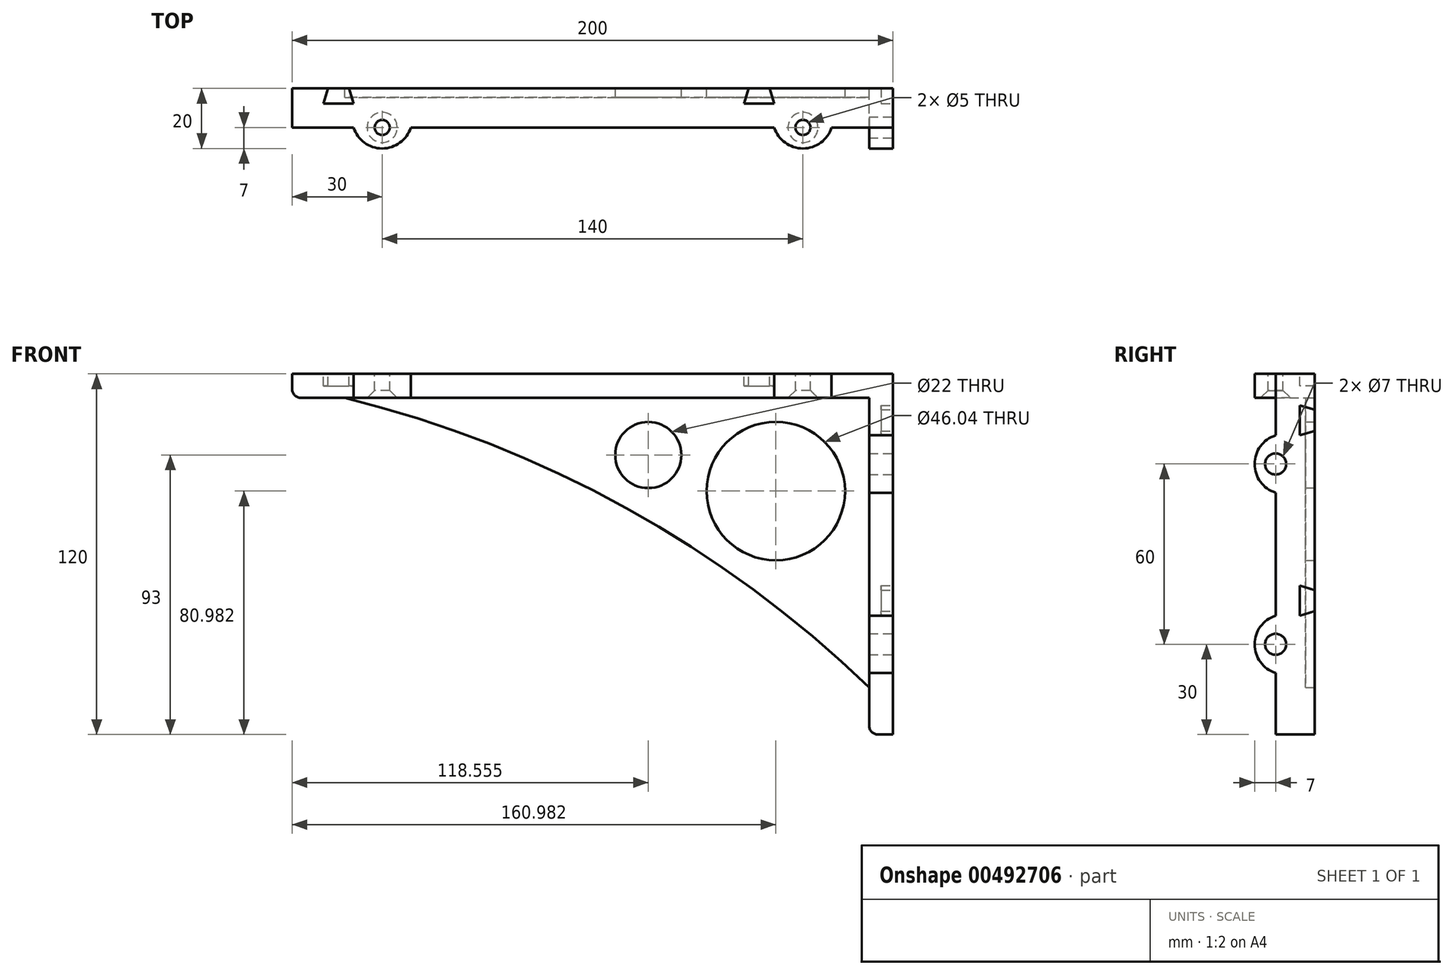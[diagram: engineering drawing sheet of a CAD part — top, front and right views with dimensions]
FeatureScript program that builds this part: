
annotation { "Feature Type Name" : "Feature", "Feature Type Description" : "" }
export const myFeature = defineFeature(function(context is Context, id is Id, definition is map)
    precondition{}
    {
        {
            var Q0;
            Q0=qCreatedBy(makeId("Front.planeOp"),FACE);
            var sketch = newSketch(context, id + "F0", { "sketchPlane" : qUnion([Q0])});
            skLineSegment(sketch, "E0", {"start": v(0, 150.58) * mm, "end": v(0, -150.58) * mm, "construction": true});
            skLineSegment(sketch, "E1", {"start": v(52, 0) * mm, "end": v(-5, 0) * mm, "construction": true});
            skLineSegment(sketch, "E2.bottom", {"start": v(-200, 120) * mm, "end": v(0, 120) * mm});
            skLineSegment(sketch, "E2.top", {"start": v(-197, 112) * mm, "end": v(-8, 112) * mm});
            skLineSegment(sketch, "E2.left", {"start": v(-200, 120) * mm, "end": v(-200, 115) * mm});
            skLineSegment(sketch, "E3.top", {"start": v(-8, 0) * mm, "end": v(0, 0) * mm});
            skLineSegment(sketch, "E3.left", {"start": v(-8, 112) * mm, "end": v(-8, 3) * mm});
            skLineSegment(sketch, "E4", {"start": v(0, 120) * mm, "end": v(0, 0) * mm});
            skCircle(sketch, "E5", {"center": v(-39.02, 80.98) * mm, "radius": 23.02 * mm});
            skLineSegment(sketch, "E6", {"start": v(0, 120) * mm, "end": v(-8, 112) * mm, "construction": true});
            skLineSegment(sketch, "E7", {"start": v(-8, 112) * mm, "end": v(-70.48, 49.52) * mm, "construction": true});
            skCircle(sketch, "E8", {"center": v(-81.45, 93) * mm, "radius": 11 * mm});
            skArc(sketch, "E9", {"start": v(-8, 15.64) * mm, "mid": v(-88.84, 75.38) * mm, "end": v(-182.45, 112) * mm});
            skPoint(sketch, "E10.visualSharp", {"position": v(-200, 112) * mm});
            skArc(sketch, "E10.filletArc", {"start": v(-200, 115) * mm, "mid": v(-199.12, 112.88) * mm, "end": v(-197, 112) * mm});
            skArc(sketch, "E11.filletArc", {"start": v(-8, 3) * mm, "mid": v(-7.12, 0.88) * mm, "end": v(-5, 0) * mm});
            skLineSegment(sketch, "E12", {"start": v(-210.09, 116) * mm, "end": v(15.72, 116) * mm, "construction": true});
            skLineSegment(sketch, "E13", {"start": v(-4, 123.59) * mm, "end": v(-4, 7.46) * mm, "construction": true});
            skPoint(sketch, "E13.endSnap0", {"position": v(-4, 0) * mm});
            skSolve(sketch);
        }
        {
            var Q0;
            Q0=makeQuery(id+"F0.imprint","IMPRINT",FACE,{"disambiguationData":[TD([[makeQuery(id+"F0.imprint","IMPRINT",EDGE,{"derivedFrom":sQuery(id+"F0.wireOp",EDGE,"E5")}),-1.0]])]});
            extrude(context, id + "F1", {"entities" : qUnion([Q0]), "depth" : 3 * mm});
        }
        {
            var Q0;
            Q0=makeQuery(id+"F0.imprint","IMPRINT",FACE,{"disambiguationData":[TD([[makeQuery(id+"F0.imprint","IMPRINT",EDGE,{"derivedFrom":sQuery(id+"F0.wireOp",EDGE,"E2.bottom")}),-1.0]])]});
            extrude(context, id + "F2", {"entities" : qUnion([Q0]), "depth" : 20 * mm});
        }
        {
            var Q0;
            Q0=qCreatedBy(makeId("Right.planeOp"),FACE);
            var sketch = newSketch(context, id + "F3", { "sketchPlane" : qUnion([Q0])});
            skLineSegment(sketch, "E14", {"start": v(0, 131.94) * mm, "end": v(0, -6.13) * mm, "construction": true});
            skLineSegment(sketch, "E15", {"start": v(28.25, 0) * mm, "end": v(-74.04, 0) * mm, "construction": true});
            skLineSegment(sketch, "E16", {"start": v(-10, 123.32) * mm, "end": v(-10, 3.6) * mm, "construction": true});
            skCircle(sketch, "E17", {"center": v(-10, 90) * mm, "radius": 10 * mm});
            skCircle(sketch, "E18.1.0.0", {"center": v(-10, 30) * mm, "radius": 10 * mm});
            skLineSegment(sketch, "E18.direction1", {"start": v(-10, 90) * mm, "end": v(-10, 30) * mm, "construction": true});
            skLineSegment(sketch, "E19", {"start": v(-13, 124.76) * mm, "end": v(-13, -7.06) * mm, "construction": true});
            skCircle(sketch, "E20", {"center": v(-13, 90) * mm, "radius": 3.5 * mm});
            skCircle(sketch, "E21", {"center": v(-13, 30) * mm, "radius": 3.5 * mm});
            skLineSegment(sketch, "E22.0", {"start": v(-20, 120) * mm, "end": v(0, 120) * mm});
            skLineSegment(sketch, "E23.0", {"start": v(-20, 120) * mm, "end": v(-20, 0) * mm});
            skLineSegment(sketch, "E24.0.0", {"start": v(0, 0) * mm, "end": v(0, 120) * mm});
            skLineSegment(sketch, "E24.0.1", {"start": v(0, 120) * mm, "end": v(-20, 120) * mm});
            skLineSegment(sketch, "E24.0.3", {"start": v(-20, 0) * mm, "end": v(0, 0) * mm});
            skLineSegment(sketch, "E25", {"start": v(-13, 120) * mm, "end": v(-13, 99.54) * mm});
            skLineSegment(sketch, "E26", {"start": v(-13, 80.46) * mm, "end": v(-13, 39.54) * mm});
            skLineSegment(sketch, "E27", {"start": v(-13, 20.46) * mm, "end": v(-13, 0) * mm});
            skSolve(sketch);
        }
        {
            var Q0;
            {var subQ0=sQuery(id+"F3.wireOp",EDGE,"E27");Q0=makeQuery(id+"F3.imprint","IMPRINT",FACE,{"disambiguationData":[TD([[makeQuery(id+"F3.imprint","IMPRINT",EDGE,{"derivedFrom":subQ0}),-1.0]])]});}
            var Q1;
            {var subQ0=sQuery(id+"F3.wireOp",EDGE,"E26");Q1=makeQuery(id+"F3.imprint","IMPRINT",FACE,{"disambiguationData":[TD([[makeQuery(id+"F3.imprint","IMPRINT",EDGE,{"derivedFrom":subQ0}),-1.0]])]});}
            var Q2;
            {var subQ0=sQuery(id+"F3.wireOp",EDGE,"E25");Q2=makeQuery(id+"F3.imprint","IMPRINT",FACE,{"disambiguationData":[TD([[makeQuery(id+"F3.imprint","IMPRINT",EDGE,{"derivedFrom":subQ0}),-1.0]])]});}
            var Q3;
            Q3=makeQuery(id+"F3.imprint","IMPRINT",FACE,{"disambiguationData":[TD([[makeQuery(id+"F3.imprint","IMPRINT",EDGE,{"derivedFrom":sQuery(id+"F3.wireOp",EDGE,"E20")}),1.0]])]});
            var Q4;
            Q4=makeQuery(id+"F3.imprint","IMPRINT",FACE,{"disambiguationData":[TD([[makeQuery(id+"F3.imprint","IMPRINT",EDGE,{"derivedFrom":sQuery(id+"F3.wireOp",EDGE,"E21")}),1.0]])]});
            extrude(context, id + "F4", {"entities" : qUnion([Q0, Q1, Q2, Q3, Q4]), "operationType" : NewBodyOperationType.REMOVE, "oppositeDirection" : true, "depth" : 10 * mm});
        }
        {
            var Q0;
            Q0=makeQuery(id+"F2.opExtrude","SWEPT_FACE",FACE,{"disambiguationData":[OSD([sQuery(id+"F0.wireOp",EDGE,"E4")])]});
            var sketch = newSketch(context, id + "F5", { "sketchPlane" : qUnion([Q0])});
            skLineSegment(sketch, "E28", {"start": v(0, 114.7) * mm, "end": v(0, -4.87) * mm, "construction": true});
            skLineSegment(sketch, "E29", {"start": v(-17.8, 0) * mm, "end": v(12.61, 0) * mm, "construction": true});
            skLineSegment(sketch, "E30", {"start": v(-13, 99.54) * mm, "end": v(6.7, 99.54) * mm, "construction": true});
            skLineSegment(sketch, "E31", {"start": v(-13, 39.54) * mm, "end": v(7.65, 39.54) * mm, "construction": true});
            skLineSegment(sketch, "E32", {"start": v(0, 108.04) * mm, "end": v(-5, 109.54) * mm});
            skLineSegment(sketch, "E33", {"start": v(-5, 109.54) * mm, "end": v(-5, 99.54) * mm});
            skLineSegment(sketch, "E34", {"start": v(-5, 99.54) * mm, "end": v(0, 101.04) * mm});
            skLineSegment(sketch, "E35", {"start": v(0, 108.04) * mm, "end": v(0, 101.04) * mm});
            skLineSegment(sketch, "E36", {"start": v(3.72, 104.54) * mm, "end": v(-16.38, 104.54) * mm, "construction": true});
            skLineSegment(sketch, "E37", {"start": v(0, 48.04) * mm, "end": v(-5, 49.54) * mm});
            skLineSegment(sketch, "E38", {"start": v(-5, 49.54) * mm, "end": v(-5, 39.54) * mm});
            skLineSegment(sketch, "E39", {"start": v(-5, 39.54) * mm, "end": v(0, 41.04) * mm});
            skLineSegment(sketch, "E40", {"start": v(0, 48.04) * mm, "end": v(0, 41.04) * mm});
            skLineSegment(sketch, "E41", {"start": v(1.78, 44.54) * mm, "end": v(-18.33, 44.54) * mm, "construction": true});
            skSolve(sketch);
        }
        {
            var Q0;
            Q0=makeQuery(id+"F5.imprint","IMPRINT",FACE,{"disambiguationData":[TD([[makeQuery(id+"F5.imprint","IMPRINT",EDGE,{"derivedFrom":sQuery(id+"F5.wireOp",EDGE,"E32")}),1.0]])]});
            var Q1;
            Q1=makeQuery(id+"F5.imprint","IMPRINT",FACE,{"disambiguationData":[TD([[makeQuery(id+"F5.imprint","IMPRINT",EDGE,{"derivedFrom":sQuery(id+"F5.wireOp",EDGE,"E37")}),1.0]])]});
            extrude(context, id + "F6", {"entities" : qUnion([Q0, Q1]), "operationType" : NewBodyOperationType.REMOVE, "oppositeDirection" : true, "depth" : 4 * mm});
        }
        {
            var Q0;
            Q0=makeQuery(id+"F2.opExtrude","SWEPT_FACE",FACE,{"disambiguationData":[OSD([sQuery(id+"F0.wireOp",EDGE,"E2.bottom")])]});
            var sketch = newSketch(context, id + "F7", { "sketchPlane" : qUnion([Q0])});
            skLineSegment(sketch, "E42", {"start": v(-215.12, 0) * mm, "end": v(6.13, 0) * mm, "construction": true});
            skLineSegment(sketch, "E43", {"start": v(0, 28.25) * mm, "end": v(0, -74.04) * mm, "construction": true});
            skLineSegment(sketch, "E44", {"start": v(-203.32, -10) * mm, "end": v(-83.6, -10) * mm, "construction": true});
            skCircle(sketch, "E45", {"center": v(-170, -10) * mm, "radius": 10 * mm});
            skCircle(sketch, "E46.1.0.0", {"center": v(-30, -10) * mm, "radius": 10 * mm});
            skLineSegment(sketch, "E46.direction1", {"start": v(-170, -10) * mm, "end": v(-30, -10) * mm, "construction": true});
            skLineSegment(sketch, "E47", {"start": v(-204.76, -13) * mm, "end": v(-72.94, -13) * mm, "construction": true});
            skCircle(sketch, "E48", {"center": v(-170, -13) * mm, "radius": 2.5 * mm});
            skCircle(sketch, "E49", {"center": v(-30, -13) * mm, "radius": 2.5 * mm});
            skLineSegment(sketch, "E50.0", {"start": v(-200, -20) * mm, "end": v(-200, 0) * mm});
            skLineSegment(sketch, "E51.0", {"start": v(-200, -20) * mm, "end": v(0, -20) * mm});
            skLineSegment(sketch, "E52.0.0", {"start": v(0, 0) * mm, "end": v(-200, 0) * mm});
            skLineSegment(sketch, "E52.0.1", {"start": v(-200, 0) * mm, "end": v(-200, -20) * mm});
            skLineSegment(sketch, "E52.0.3", {"start": v(0, -20) * mm, "end": v(0, 0) * mm});
            skLineSegment(sketch, "E53", {"start": v(-200, -13) * mm, "end": v(-179.54, -13) * mm});
            skLineSegment(sketch, "E54", {"start": v(-160.46, -13) * mm, "end": v(-39.54, -13) * mm});
            skLineSegment(sketch, "E55", {"start": v(-20.46, -13) * mm, "end": v(0, -13) * mm});
            skLineSegment(sketch, "E56", {"start": v(-114.7, 0) * mm, "end": v(4.87, 0) * mm, "construction": true});
            skLineSegment(sketch, "E57", {"start": v(0, -17.8) * mm, "end": v(0, 12.61) * mm, "construction": true});
            skLineSegment(sketch, "E58", {"start": v(-179.54, -13) * mm, "end": v(-179.54, 6.7) * mm, "construction": true});
            skLineSegment(sketch, "E59", {"start": v(-39.54, -13) * mm, "end": v(-39.54, 7.65) * mm, "construction": true});
            skLineSegment(sketch, "E60", {"start": v(-188.04, 0) * mm, "end": v(-189.54, -5) * mm});
            skLineSegment(sketch, "E61", {"start": v(-189.54, -5) * mm, "end": v(-179.54, -5) * mm});
            skLineSegment(sketch, "E62", {"start": v(-179.54, -5) * mm, "end": v(-181.04, 0) * mm});
            skLineSegment(sketch, "E63", {"start": v(-188.04, 0) * mm, "end": v(-181.04, 0) * mm});
            skLineSegment(sketch, "E64", {"start": v(-184.54, 3.72) * mm, "end": v(-184.54, -16.38) * mm, "construction": true});
            skLineSegment(sketch, "E65", {"start": v(-48.04, 0) * mm, "end": v(-49.54, -5) * mm});
            skLineSegment(sketch, "E66", {"start": v(-49.54, -5) * mm, "end": v(-39.54, -5) * mm});
            skLineSegment(sketch, "E67", {"start": v(-39.54, -5) * mm, "end": v(-41.04, 0) * mm});
            skLineSegment(sketch, "E68", {"start": v(-48.04, 0) * mm, "end": v(-41.04, 0) * mm});
            skLineSegment(sketch, "E69", {"start": v(-44.54, 1.78) * mm, "end": v(-44.54, -18.33) * mm, "construction": true});
            skSolve(sketch);
        }
        {
            var Q0;
            {var subQ3=sQuery(id+"F7.wireOp",EDGE,"E53");Q0=makeQuery(id+"F7.imprint","IMPRINT",FACE,{"disambiguationData":[TD([[makeQuery(id+"F7.imprint","IMPRINT",EDGE,{"derivedFrom":subQ3}),-1.0]])]});}
            var Q1;
            Q1=makeQuery(id+"F7.imprint","IMPRINT",FACE,{"disambiguationData":[TD([[makeQuery(id+"F7.imprint","IMPRINT",EDGE,{"derivedFrom":sQuery(id+"F7.wireOp",EDGE,"E48")}),1.0]])]});
            var Q2;
            Q2=makeQuery(id+"F7.imprint","IMPRINT",FACE,{"disambiguationData":[TD([[makeQuery(id+"F7.imprint","IMPRINT",EDGE,{"derivedFrom":sQuery(id+"F7.wireOp",EDGE,"E49")}),1.0]])]});
            extrude(context, id + "F8", {"entities" : qUnion([Q0, Q1, Q2]), "operationType" : NewBodyOperationType.REMOVE, "oppositeDirection" : true, "depth" : 10 * mm});
        }
        {
            var Q0;
            Q0=makeQuery(id+"F2.opExtrude","SWEPT_FACE",FACE,{"disambiguationData":[OSD([sQuery(id+"F0.wireOp",EDGE,"E2.bottom")])]});
            var sketch = newSketch(context, id + "F9", { "sketchPlane" : qUnion([Q0])});
            skLineSegment(sketch, "E70", {"start": v(-215.12, 0) * mm, "end": v(6.13, 0) * mm, "construction": true});
            skLineSegment(sketch, "E71", {"start": v(0, 28.25) * mm, "end": v(0, -74.04) * mm, "construction": true});
            skLineSegment(sketch, "E72", {"start": v(-203.32, -10) * mm, "end": v(-83.6, -10) * mm, "construction": true});
            skCircle(sketch, "E73", {"center": v(-170, -10) * mm, "radius": 10 * mm});
            skCircle(sketch, "E74.1.0.0", {"center": v(-30, -10) * mm, "radius": 10 * mm});
            skLineSegment(sketch, "E74.direction1", {"start": v(-170, -10) * mm, "end": v(-30, -10) * mm, "construction": true});
            skLineSegment(sketch, "E75", {"start": v(-204.76, -13) * mm, "end": v(-72.94, -13) * mm, "construction": true});
            skCircle(sketch, "E76", {"center": v(-170, -13) * mm, "radius": 3.5 * mm});
            skCircle(sketch, "E77", {"center": v(-30, -13) * mm, "radius": 3.5 * mm});
            skLineSegment(sketch, "E78.0", {"start": v(-200, -20) * mm, "end": v(-200, 0) * mm});
            skLineSegment(sketch, "E79.0", {"start": v(-200, -20) * mm, "end": v(0, -20) * mm});
            skLineSegment(sketch, "E80.0.0", {"start": v(0, 0) * mm, "end": v(-200, 0) * mm});
            skLineSegment(sketch, "E80.0.1", {"start": v(-200, 0) * mm, "end": v(-200, -20) * mm});
            skLineSegment(sketch, "E80.0.3", {"start": v(0, -20) * mm, "end": v(0, 0) * mm});
            skLineSegment(sketch, "E81", {"start": v(-200, -13) * mm, "end": v(-179.54, -13) * mm});
            skLineSegment(sketch, "E82", {"start": v(-160.46, -13) * mm, "end": v(-39.54, -13) * mm});
            skLineSegment(sketch, "E83", {"start": v(-20.46, -13) * mm, "end": v(0, -13) * mm});
            skLineSegment(sketch, "E84", {"start": v(-114.7, 0) * mm, "end": v(4.87, 0) * mm, "construction": true});
            skLineSegment(sketch, "E85", {"start": v(0, -17.8) * mm, "end": v(0, 12.61) * mm, "construction": true});
            skLineSegment(sketch, "E86", {"start": v(-179.54, -13) * mm, "end": v(-179.54, 6.7) * mm, "construction": true});
            skLineSegment(sketch, "E87", {"start": v(-39.54, -13) * mm, "end": v(-39.54, 7.65) * mm, "construction": true});
            skLineSegment(sketch, "E88", {"start": v(-188.04, 0) * mm, "end": v(-189.54, -5) * mm});
            skLineSegment(sketch, "E89", {"start": v(-189.54, -5) * mm, "end": v(-179.54, -5) * mm});
            skLineSegment(sketch, "E90", {"start": v(-179.54, -5) * mm, "end": v(-181.04, 0) * mm});
            skLineSegment(sketch, "E91", {"start": v(-188.04, 0) * mm, "end": v(-181.04, 0) * mm});
            skLineSegment(sketch, "E92", {"start": v(-184.54, 3.72) * mm, "end": v(-184.54, -16.38) * mm, "construction": true});
            skLineSegment(sketch, "E93", {"start": v(-48.04, 0) * mm, "end": v(-49.54, -5) * mm});
            skLineSegment(sketch, "E94", {"start": v(-49.54, -5) * mm, "end": v(-39.54, -5) * mm});
            skLineSegment(sketch, "E95", {"start": v(-39.54, -5) * mm, "end": v(-41.04, 0) * mm});
            skLineSegment(sketch, "E96", {"start": v(-48.04, 0) * mm, "end": v(-41.04, 0) * mm});
            skLineSegment(sketch, "E97", {"start": v(-44.54, 1.78) * mm, "end": v(-44.54, -18.33) * mm, "construction": true});
            skSolve(sketch);
        }
        {
            var Q0;
            Q0=makeQuery(id+"F9.imprint","IMPRINT",FACE,{"disambiguationData":[TD([[makeQuery(id+"F9.imprint","IMPRINT",EDGE,{"derivedFrom":sQuery(id+"F9.wireOp",EDGE,"E88")}),1.0]])]});
            var Q1;
            Q1=makeQuery(id+"F9.imprint","IMPRINT",FACE,{"disambiguationData":[TD([[makeQuery(id+"F9.imprint","IMPRINT",EDGE,{"derivedFrom":sQuery(id+"F9.wireOp",EDGE,"E93")}),1.0]])]});
            extrude(context, id + "F10", {"entities" : qUnion([Q0, Q1]), "operationType" : NewBodyOperationType.REMOVE, "oppositeDirection" : true, "depth" : 4 * mm});
        }
        {
            var Q0;
            Q0=makeQuery(id+"F8.boolean.opBoolean","INTERSECT",EDGE,{"derivedFrom":[makeQuery(id+"F2.opExtrude","SWEPT_FACE",FACE,{"disambiguationData":[OSD([sQuery(id+"F0.wireOp",EDGE,"E2.top")])]}),makeQuery(id+"F8.opExtrude","SWEPT_FACE",FACE,{"disambiguationData":[OSD([sQuery(id+"F7.wireOp",EDGE,"E48")])]})]});
            var Q1;
            Q1=makeQuery(id+"F8.boolean.opBoolean","INTERSECT",EDGE,{"derivedFrom":[makeQuery(id+"F2.opExtrude","SWEPT_FACE",FACE,{"disambiguationData":[OSD([sQuery(id+"F0.wireOp",EDGE,"E2.top")])]}),makeQuery(id+"F8.opExtrude","SWEPT_FACE",FACE,{"disambiguationData":[OSD([sQuery(id+"F7.wireOp",EDGE,"E49")])]})]});
            chamfer(context, id + "F11", {"entities" : qUnion([Q0, Q1]), "chamferType" : ChamferType.OFFSET_ANGLE, "width" : 2.5 * mm, "oppositeDirection" : false, "angle" : 45 * degree, "tangentPropagation" : true});
        }
    });
